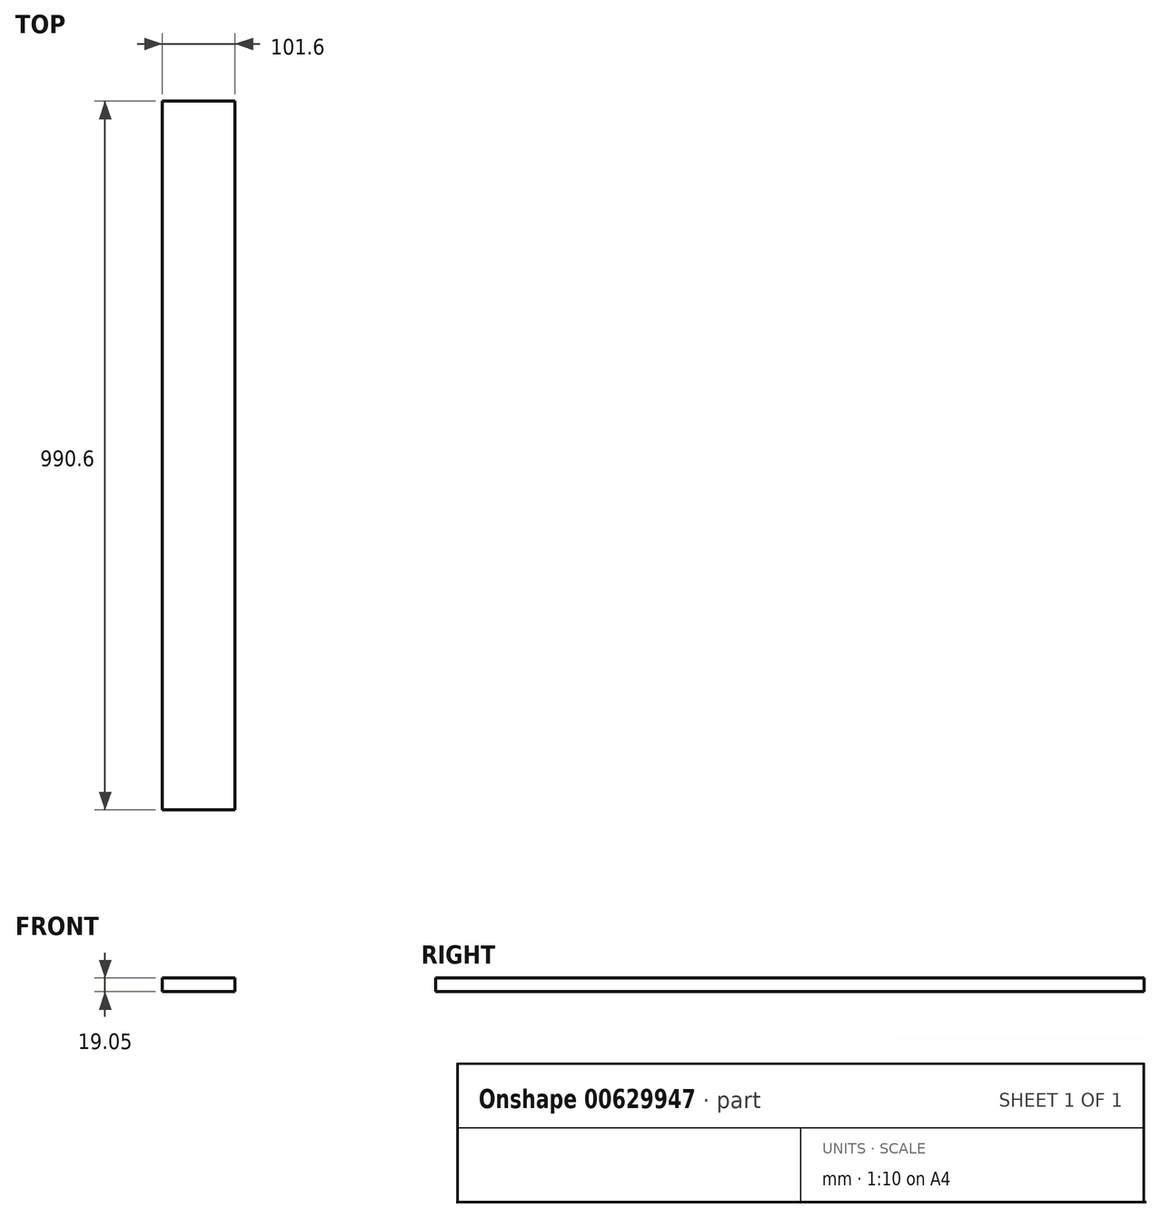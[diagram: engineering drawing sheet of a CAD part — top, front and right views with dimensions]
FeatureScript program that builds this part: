
annotation { "Feature Type Name" : "Feature", "Feature Type Description" : "" }
export const myFeature = defineFeature(function(context is Context, id is Id, definition is map)
    precondition{}
    {
        {
            var Q0;
            Q0=qCreatedBy(makeId("Front.planeOp"),FACE);
            var sketch = newSketch(context, id + "F0", { "sketchPlane" : qUnion([Q0])});
            skLineSegment(sketch, "E0.bottom", {"start": v(-69.37, 19.05) * mm, "end": v(32.23, 19.05) * mm});
            skLineSegment(sketch, "E0.top", {"start": v(-69.37, 0) * mm, "end": v(32.23, 0) * mm});
            skLineSegment(sketch, "E0.left", {"start": v(-69.37, 19.05) * mm, "end": v(-69.37, 0) * mm});
            skLineSegment(sketch, "E0.right", {"start": v(32.23, 19.05) * mm, "end": v(32.23, 0) * mm});
            skSolve(sketch);
        }
        {
            var Q0;
            Q0=makeQuery(id+"F0.imprint","IMPRINT",FACE,{"disambiguationData":[TD([[makeQuery(id+"F0.imprint","IMPRINT",EDGE,{"derivedFrom":sQuery(id+"F0.wireOp",EDGE,"E0.bottom")}),-1.0]])]});
            extrude(context, id + "F1", {"entities" : qUnion([Q0]), "depth" : 990.6 * mm, "offsetDistance" : 25.4 * mm});
        }
    });
